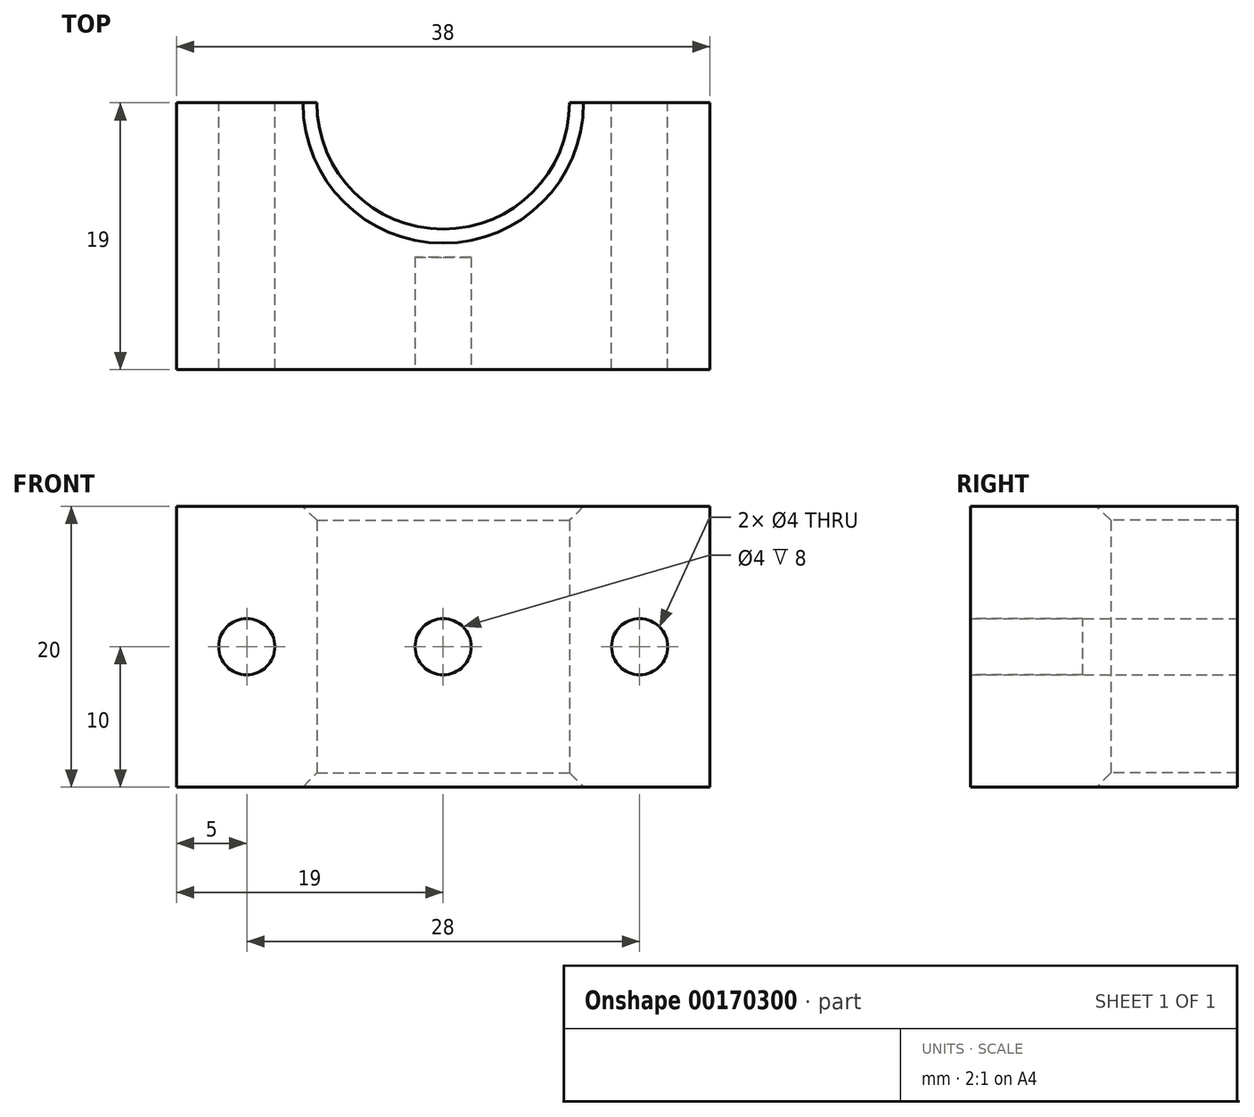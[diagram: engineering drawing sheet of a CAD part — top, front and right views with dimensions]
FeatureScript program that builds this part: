
annotation { "Feature Type Name" : "Feature", "Feature Type Description" : "" }
export const myFeature = defineFeature(function(context is Context, id is Id, definition is map)
    precondition{}
    {
        {
            var Q0;
            Q0=qCreatedBy(makeId("Top.planeOp"),FACE);
            var sketch = newSketch(context, id + "F0", { "sketchPlane" : qUnion([Q0])});
            skLineSegment(sketch, "E0.bottom", {"start": v(-19, 9.5) * mm, "end": v(-9, 9.5) * mm});
            skLineSegment(sketch, "E0.top", {"start": v(-19, -9.5) * mm, "end": v(19, -9.5) * mm});
            skLineSegment(sketch, "E0.left", {"start": v(-19, 9.5) * mm, "end": v(-19, -9.5) * mm});
            skLineSegment(sketch, "E0.right", {"start": v(19, 9.5) * mm, "end": v(19, -9.5) * mm});
            skArc(sketch, "E1", {"start": v(-9, 9.5) * mm, "mid": v(0, 0.5) * mm, "end": v(9, 9.5) * mm});
            skLineSegment(sketch, "E2.trimOffspring", {"start": v(9, 9.5) * mm, "end": v(19, 9.5) * mm});
            skSolve(sketch);
        }
        {
            var Q0;
            Q0=qSketchRegion(id+"F0",true);
            extrude(context, id + "F1", {"entities" : qUnion([Q0]), "depth" : 20 * mm});
        }
        {
            var Q0;
            Q0=makeQuery(id+"F1.opExtrude","SWEPT_FACE",FACE,{"disambiguationData":[OSD([sQuery(id+"F0.wireOp",EDGE,"E0.bottom")])]});
            var sketch = newSketch(context, id + "F2", { "sketchPlane" : qUnion([Q0])});
            skCircle(sketch, "E3", {"center": v(-14, 10) * mm, "radius": 2 * mm});
            skCircle(sketch, "E4", {"center": v(14, 10) * mm, "radius": 2 * mm});
            skSolve(sketch);
        }
        {
            var Q0;
            Q0=qSketchRegion(id+"F2",true);
            extrude(context, id + "F3", {"entities" : qUnion([Q0]), "operationType" : NewBodyOperationType.REMOVE, "endBound" : BoundingType.THROUGH_ALL, "oppositeDirection" : true, "depth" : 25 * mm});
        }
        {
            var Q0;
            Q0=makeQuery(id+"F1.opExtrude","SWEPT_FACE",FACE,{"disambiguationData":[OSD([sQuery(id+"F0.wireOp",EDGE,"E0.top")])]});
            var sketch = newSketch(context, id + "F4", { "sketchPlane" : qUnion([Q0])});
            skCircle(sketch, "E5", {"center": v(0, 10) * mm, "radius": 2 * mm});
            skSolve(sketch);
        }
        {
            var Q0;
            Q0 = qSketchRegion(id + "F4", true);
            extrude(context, id + "F5", {"entities" : qUnion([Q0]), "operationType" : NewBodyOperationType.REMOVE, "oppositeDirection" : true, "depth" : 8 * mm});
        }
        {
            var Q0;
            Q0=makeQuery(id+"F1.opExtrude","CAP_EDGE",EDGE,{"disambiguationData":[OSD([sQuery(id+"F0.wireOp",EDGE,"E1")])],"isStart":true});
            var Q1;
            Q1=makeQuery(id+"F1.opExtrude","CAP_EDGE",EDGE,{"disambiguationData":[OSD([sQuery(id+"F0.wireOp",EDGE,"E1")])],"isStart":false});
            chamfer(context, id + "F6", {"entities" : qUnion([Q0, Q1]), "width" : 1 * mm, "tangentPropagation" : true});
        }
    });
